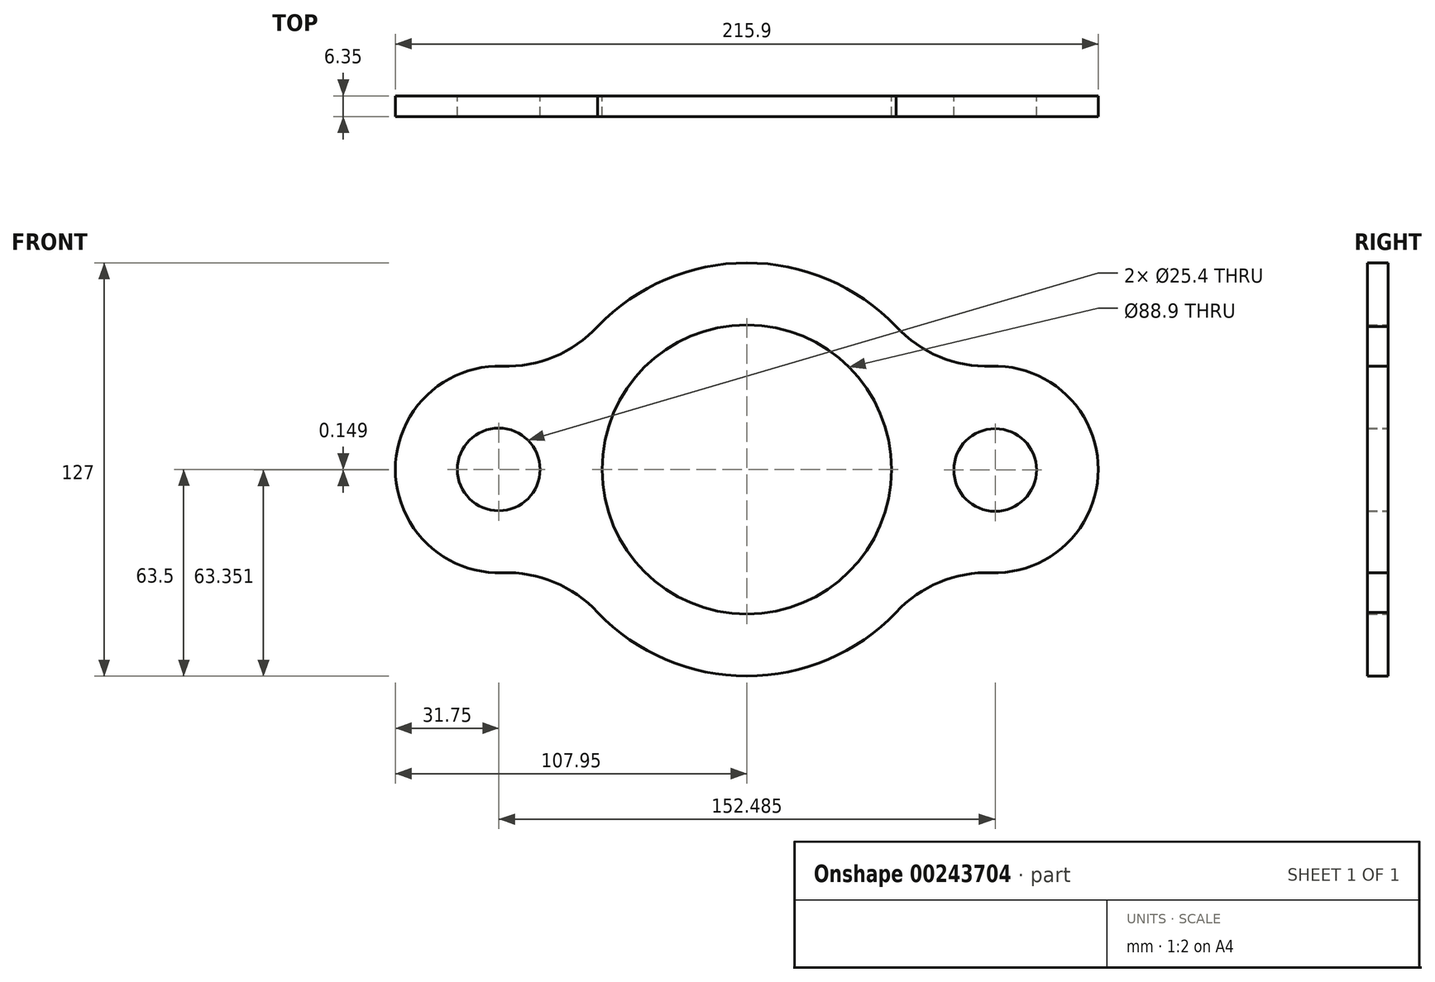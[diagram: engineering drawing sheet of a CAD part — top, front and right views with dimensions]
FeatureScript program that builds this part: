
annotation { "Feature Type Name" : "Feature", "Feature Type Description" : "" }
export const myFeature = defineFeature(function(context is Context, id is Id, definition is map)
    precondition{}
    {
        {
            var Q0;
            Q0=qCreatedBy(makeId("Front.planeOp"),FACE);
            var sketch = newSketch(context, id + "F0", { "sketchPlane" : qUnion([Q0])});
            skCircle(sketch, "E0", {"center": v(0, 0) * mm, "radius": 44.45 * mm});
            skCircle(sketch, "E1", {"center": v(-76.2, 0) * mm, "radius": 12.7 * mm});
            skCircle(sketch, "E2", {"center": v(76.29, -0.15) * mm, "radius": 12.7 * mm});
            skArc(sketch, "E3", {"start": v(-75.12, 31.73) * mm, "mid": v(-107.95, 0) * mm, "end": v(-75.12, -31.73) * mm});
            skArc(sketch, "E4.filletArc", {"start": v(-75.12, 31.73) * mm, "mid": v(-59.14, 34.65) * mm, "end": v(-45.83, 43.96) * mm});
            skLineSegment(sketch, "E5", {"start": v(58.09, 25.65) * mm, "end": v(58.09, 25.65) * mm});
            skArc(sketch, "E6", {"start": v(46.15, 43.61) * mm, "mid": v(0.24, 63.5) * mm, "end": v(-45.83, 43.96) * mm});
            skLineSegment(sketch, "E7", {"start": v(-57.43, -25.6) * mm, "end": v(-57.43, -25.6) * mm});
            skArc(sketch, "E8.MirrorCS", {"start": v(75.12, 31.73) * mm, "mid": v(59.14, 34.65) * mm, "end": v(45.83, 43.96) * mm});
            skArc(sketch, "E9.MirrorCS", {"start": v(46.15, -43.61) * mm, "mid": v(0.24, -63.5) * mm, "end": v(-45.83, -43.96) * mm});
            skArc(sketch, "E10.MirrorCS", {"start": v(-75.12, -31.73) * mm, "mid": v(-59.14, -34.65) * mm, "end": v(-45.83, -43.96) * mm});
            skArc(sketch, "E11.MirrorCS", {"start": v(75.12, 31.73) * mm, "mid": v(107.95, 0) * mm, "end": v(75.12, -31.73) * mm});
            skArc(sketch, "E12.MirrorCS", {"start": v(75.12, -31.73) * mm, "mid": v(59.14, -34.65) * mm, "end": v(45.83, -43.96) * mm});
            skPoint(sketch, "E13", {"position": v(101.67, 18.96) * mm});
            skSolve(sketch);
        }
        {
            var Q0;
            Q0=makeQuery(id+"F0.imprint","IMPRINT",FACE,{"disambiguationData":[TD([[makeQuery(id+"F0.imprint","IMPRINT",EDGE,{"derivedFrom":sQuery(id+"F0.wireOp",EDGE,"E0")}),-1.0]])]});
            extrude(context, id + "F1", {"entities" : qUnion([Q0]), "depth" : 6.35 * mm});
        }
    });
